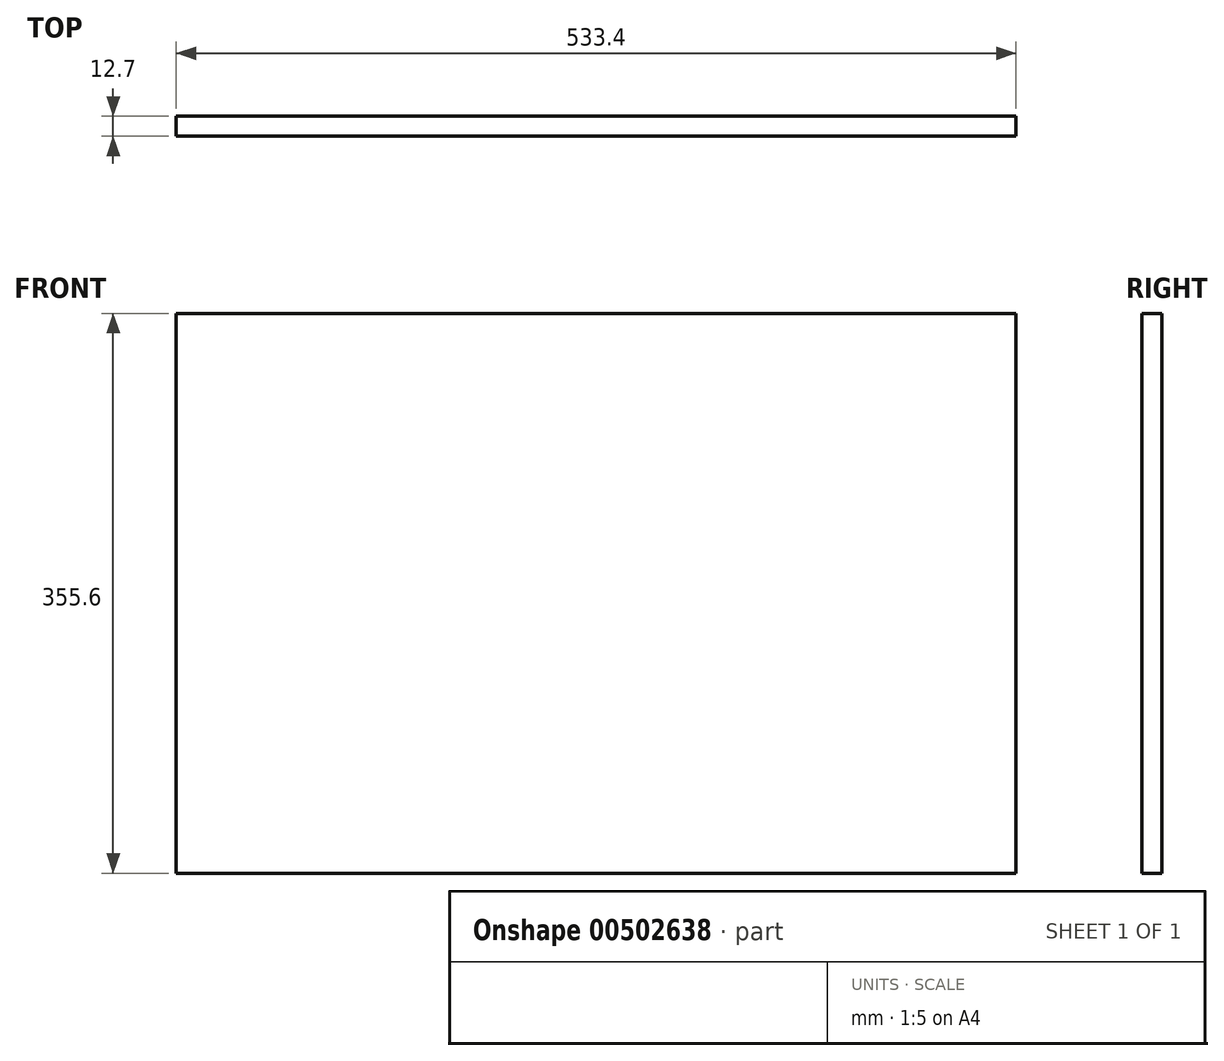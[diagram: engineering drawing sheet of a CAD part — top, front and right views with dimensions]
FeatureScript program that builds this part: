
annotation { "Feature Type Name" : "Feature", "Feature Type Description" : "" }
export const myFeature = defineFeature(function(context is Context, id is Id, definition is map)
    precondition{}
    {
        {
            var Q0;
            Q0=qCreatedBy(makeId("Front.planeOp"),FACE);
            var sketch = newSketch(context, id + "F0", { "sketchPlane" : qUnion([Q0])});
            skLineSegment(sketch, "E0.bottom", {"start": v(0, 0) * mm, "end": v(533.4, 0) * mm});
            skLineSegment(sketch, "E0.top", {"start": v(0, 355.6) * mm, "end": v(533.4, 355.6) * mm});
            skLineSegment(sketch, "E0.left", {"start": v(0, 0) * mm, "end": v(0, 355.6) * mm});
            skLineSegment(sketch, "E0.right", {"start": v(533.4, 0) * mm, "end": v(533.4, 355.6) * mm});
            skSolve(sketch);
        }
        {
            var Q0;
            Q0=makeQuery(id+"F0.imprint","IMPRINT",FACE,{"disambiguationData":[TD([[makeQuery(id+"F0.imprint","IMPRINT",EDGE,{"derivedFrom":sQuery(id+"F0.wireOp",EDGE,"E0.bottom")}),1.0]])]});
            extrude(context, id + "F1", {"entities" : qUnion([Q0]), "depth" : 12.7 * mm});
        }
    });
